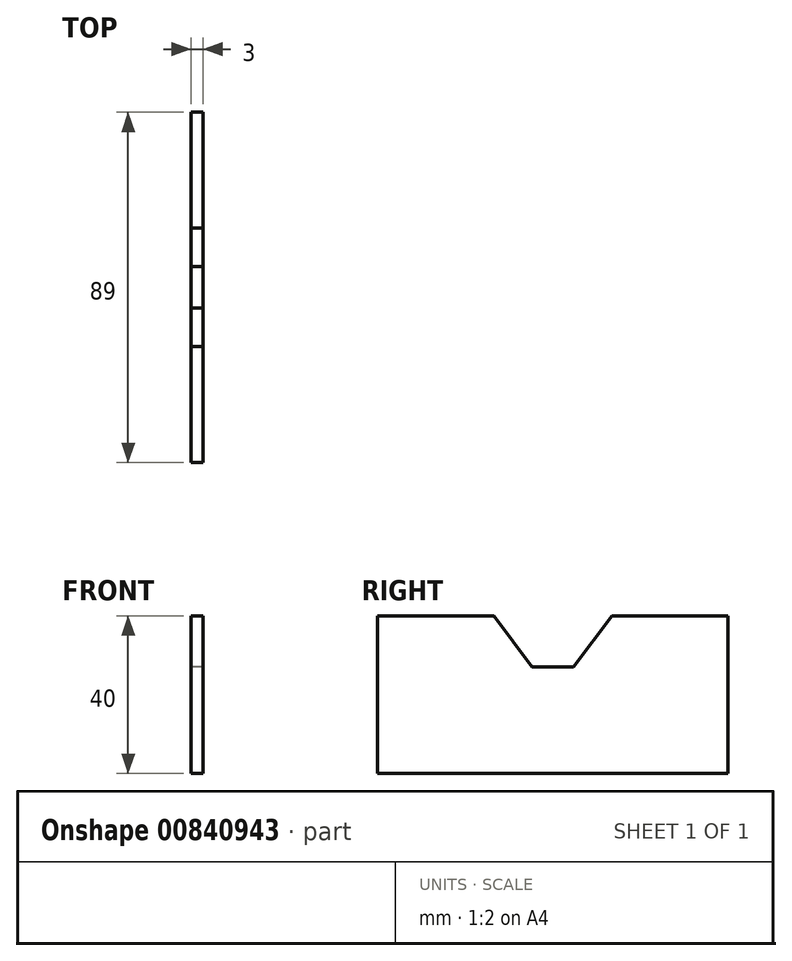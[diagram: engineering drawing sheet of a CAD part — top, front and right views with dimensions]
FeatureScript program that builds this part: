
annotation { "Feature Type Name" : "Feature", "Feature Type Description" : "" }
export const myFeature = defineFeature(function(context is Context, id is Id, definition is map)
    precondition{}
    {
        {
            var Q0;
            Q0=qCreatedBy(makeId("Right.planeOp"),FACE);
            var sketch = newSketch(context, id + "F0", { "sketchPlane" : qUnion([Q0])});
            skLineSegment(sketch, "E0", {"start": v(0, 40) * mm, "end": v(29.5, 40) * mm});
            skLineSegment(sketch, "E1", {"start": v(29.5, 40) * mm, "end": v(39.25, 27) * mm});
            skLineSegment(sketch, "E2", {"start": v(49.75, 27) * mm, "end": v(59.5, 40) * mm});
            skLineSegment(sketch, "E3", {"start": v(59.5, 40) * mm, "end": v(89, 40) * mm});
            skLineSegment(sketch, "E4", {"start": v(89, 40) * mm, "end": v(89, 0) * mm});
            skLineSegment(sketch, "E5", {"start": v(89, 0) * mm, "end": v(0, 0) * mm});
            skLineSegment(sketch, "E6", {"start": v(0, 0) * mm, "end": v(0, 40) * mm});
            skLineSegment(sketch, "E7", {"start": v(39.25, 27) * mm, "end": v(49.75, 27) * mm});
            skPoint(sketch, "E8.orphan", {"position": v(44.5, 20) * mm});
            skSolve(sketch);
        }
        {
            var Q0;
            Q0=qSketchRegion(id+"F0",true);
            extrude(context, id + "F1", {"entities" : qUnion([Q0]), "depth" : 3 * mm, "offsetDistance" : 25 * mm});
        }
    });
